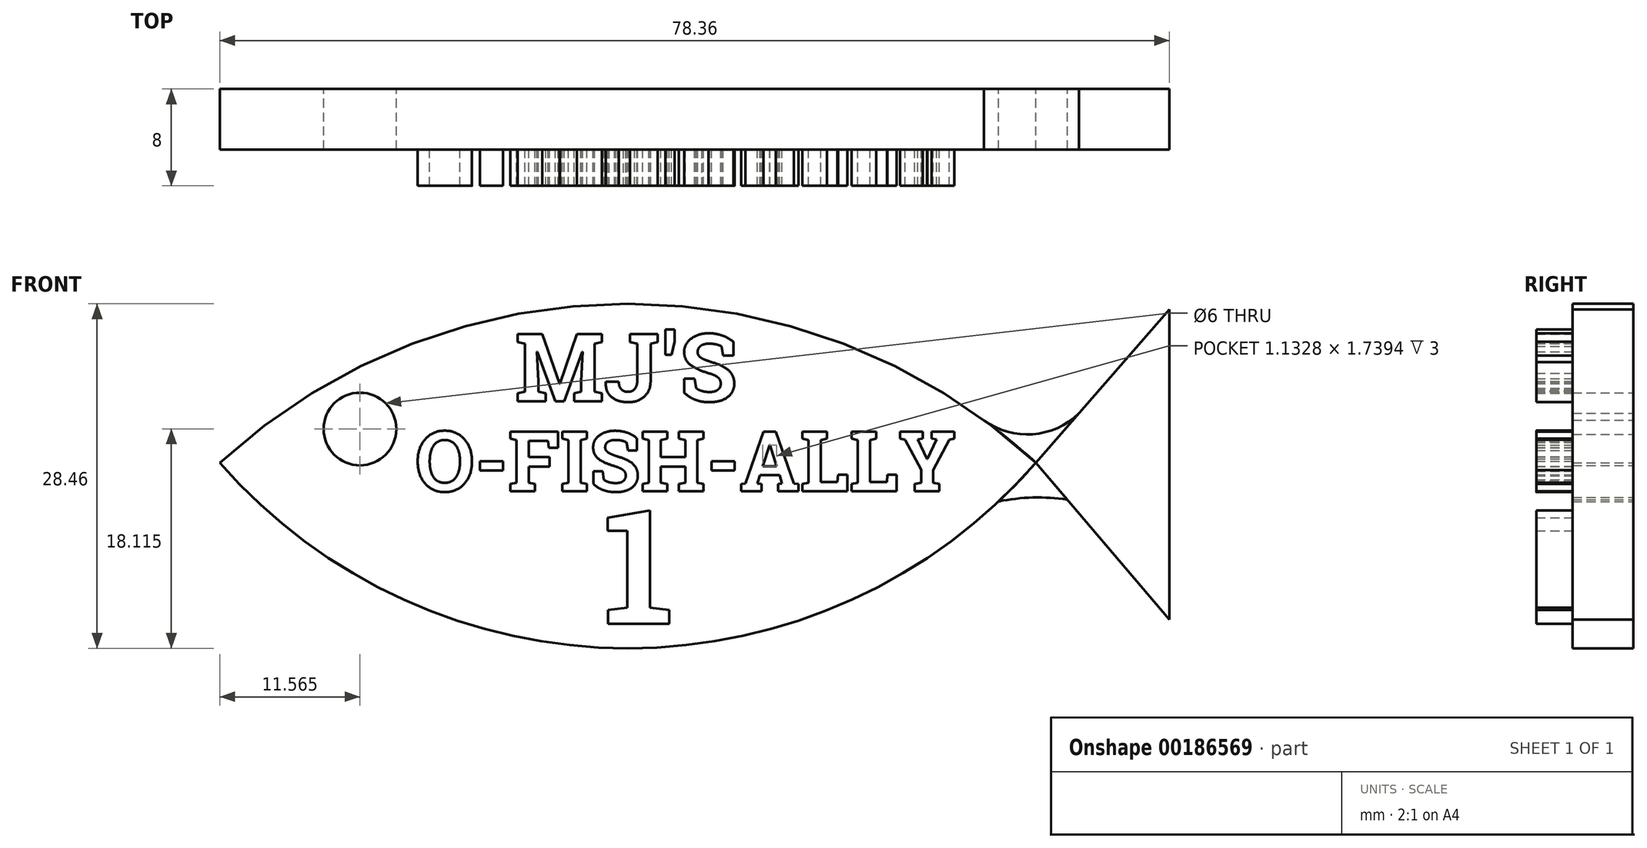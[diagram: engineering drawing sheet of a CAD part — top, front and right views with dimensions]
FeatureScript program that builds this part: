
annotation { "Feature Type Name" : "Feature", "Feature Type Description" : "" }
export const myFeature = defineFeature(function(context is Context, id is Id, definition is map)
    precondition{}
    {
        {
            var Q0;
            Q0=qCreatedBy(makeId("Front.planeOp"),FACE);
            var sketch = newSketch(context, id + "F0", { "sketchPlane" : qUnion([Q0])});
            skLineSegment(sketch, "E0.bottom", {"start": v(0, 0) * mm, "end": v(75, 0) * mm});
            skLineSegment(sketch, "E0.top", {"start": v(0, -25) * mm, "end": v(75, -25) * mm});
            skLineSegment(sketch, "E0.left", {"start": v(0, 0) * mm, "end": v(0, -25) * mm});
            skLineSegment(sketch, "E0.right", {"start": v(75, 0) * mm, "end": v(75, -25) * mm});
            skCircle(sketch, "E1", {"center": v(68, -12.5) * mm, "radius": 3.5 * mm});
            skSolve(sketch);
        }
        {
            var Q0;
            Q0=makeQuery(id+"F0.imprint","IMPRINT",FACE,{"disambiguationData":[TD([[makeQuery(id+"F0.imprint","IMPRINT",EDGE,{"derivedFrom":sQuery(id+"F0.wireOp",EDGE,"E0.bottom")}),-1.0]])]});
            extrude(context, id + "F1", {"entities" : qUnion([Q0]), "depth" : 5 * mm});
        }
        {
            var Q0;
            Q0=makeQuery(id+"F1.opExtrude","CAP_FACE",FACE,{"disambiguationData":[OSD([sQuery(id+"F0.wireOp",EDGE,"E0.bottom"),sQuery(id+"F0.wireOp",EDGE,"E0.top"),sQuery(id+"F0.wireOp",EDGE,"E0.left"),sQuery(id+"F0.wireOp",EDGE,"E0.right"),sQuery(id+"F0.wireOp",EDGE,"E1")])],"isStart":false});
            var sketch = newSketch(context, id + "F2", { "sketchPlane" : qUnion([Q0])});
            skArc(sketch, "E2", {"start": v(33.67, 61.06) * mm, "mid": v(-0.04, 74.19) * mm, "end": v(-33.73, 61) * mm});
            skArc(sketch, "E3", {"start": v(-33.73, 61.13) * mm, "mid": v(-0.05, 45.73) * mm, "end": v(33.67, 61.06) * mm});
            skLineSegment(sketch, "E4", {"start": v(33.67, 61.06) * mm, "end": v(44.7, 73.72) * mm});
            skLineSegment(sketch, "E5", {"start": v(44.7, 73.72) * mm, "end": v(44.7, 48.11) * mm});
            skLineSegment(sketch, "E6", {"start": v(44.7, 48.11) * mm, "end": v(33.67, 61.06) * mm});
            skCircle(sketch, "E7", {"center": v(-22.1, 63.85) * mm, "radius": 3 * mm});
            skArc(sketch, "E8", {"start": v(29.4, 64.57) * mm, "mid": v(33.4, 63.41) * mm, "end": v(37.22, 65.13) * mm});
            skArc(sketch, "E9", {"start": v(36.27, 58) * mm, "mid": v(33.42, 58.18) * mm, "end": v(30.6, 57.86) * mm});
            skSolve(sketch);
        }
        {
            var Q0;
            Q0=makeQuery(id+"F2.imprint","IMPRINT",FACE,{"disambiguationData":[TD([[makeQuery(id+"F2.imprint","IMPRINT",EDGE,{"derivedFrom":sQuery(id+"F2.wireOp",EDGE,"E7")}),-1.0]])]});
            var Q1;
            {var subQ1=sQuery(id+"F2.wireOp",EDGE,"E5");Q1=makeQuery(id+"F2.imprint","IMPRINT",FACE,{"disambiguationData":[TD([[makeQuery(id+"F2.imprint","IMPRINT",EDGE,{"derivedFrom":subQ1}),-1.0]])]});}
            extrude(context, id + "F3", {"entities" : qUnion([Q0, Q1]), "depth" : 5 * mm});
        }
        {
            var Q0;
            {var subQ3=sQuery(id+"F2.wireOp",EDGE,"E8");Q0=makeQuery(id+"F2.imprint","IMPRINT",FACE,{"disambiguationData":[TD([[makeQuery(id+"F2.imprint","IMPRINT",EDGE,{"derivedFrom":subQ3}),-1.0]])]});}
            extrude(context, id + "F4", {"entities" : qUnion([Q0]), "depth" : 5 * mm});
        }
        {
            var Q0;
            {var subQ3=sQuery(id+"F2.wireOp",EDGE,"E9");Q0=makeQuery(id+"F2.imprint","IMPRINT",FACE,{"disambiguationData":[TD([[makeQuery(id+"F2.imprint","IMPRINT",EDGE,{"derivedFrom":subQ3}),-1.0]])]});}
            extrude(context, id + "F5", {"entities" : qUnion([Q0]), "depth" : 5 * mm});
        }
        {
            var Q0;
            Q0=makeQuery(id+"F1.opExtrude","SWEPT_BODY",BODY,{"disambiguationData":[OSD([sQuery(id+"F0.wireOp",EDGE,"E0.bottom"),sQuery(id+"F0.wireOp",EDGE,"E0.top"),sQuery(id+"F0.wireOp",EDGE,"E0.left"),sQuery(id+"F0.wireOp",EDGE,"E0.right"),sQuery(id+"F0.wireOp",EDGE,"E1")])]});
            deleteBodies(context, id + "F6", {"entities" : qUnion([Q0])});
        }
        {
            var Q0;
            Q0=makeQuery(id+"F3.opExtrude","CAP_FACE",FACE,{"disambiguationData":[OSD([sQuery(id+"F2.wireOp",EDGE,"E2"),sQuery(id+"F2.wireOp",EDGE,"E3"),sQuery(id+"F2.wireOp",EDGE,"E7")])],"isStart":false});
            var sketch = newSketch(context, id + "F7", { "sketchPlane" : qUnion([Q0])});
            skText(sketch, "E10", { "text": "MJ\'S", "fontName": "RobotoSlab-Bold.ttf"});
            const initialGuessF7  = {"E10": [-0.0093, 0.06614, 1, 0, 0.00561]};
            skSetInitialGuess(sketch, initialGuessF7);
            skSolve(sketch);
        }
        {
            var Q0;
            Q0 = qSketchRegion(id + "F7", true);
            extrude(context, id + "F8", {"entities" : qUnion([Q0]), "operationType" : NewBodyOperationType.ADD, "depth" : 3 * mm});
        }
        {
            var Q0;
            Q0=makeQuery(id+"F3.opExtrude","CAP_FACE",FACE,{"disambiguationData":[OSD([sQuery(id+"F2.wireOp",EDGE,"E2"),sQuery(id+"F2.wireOp",EDGE,"E3"),sQuery(id+"F2.wireOp",EDGE,"E7")])],"isStart":false});
            var sketch = newSketch(context, id + "F9", { "sketchPlane" : qUnion([Q0])});
            skText(sketch, "E11", { "text": "O-FISH-ALLY", "fontName": "RobotoSlab-Bold.ttf"});
            const initialGuessF9  = {"E11": [-0.01757, 0.0587, 1, 0, 0.005]};
            skSetInitialGuess(sketch, initialGuessF9);
            skSolve(sketch);
        }
        {
            var Q0;
            Q0 = qSketchRegion(id + "F9", true);
            extrude(context, id + "F10", {"entities" : qUnion([Q0]), "operationType" : NewBodyOperationType.ADD, "depth" : 3 * mm});
        }
        {
            var Q0;
            {var subQ0=sQuery(id+"F2.wireOp",EDGE,"E2");var subQ1=sQuery(id+"F2.wireOp",EDGE,"E3");var subQ2=sQuery(id+"F2.wireOp",EDGE,"E7");Q0=makeQuery(id+"F10.boolean.opBoolean","SPLIT",FACE,{"disambiguationData":[TD([makeQuery(id+"F3.opExtrude","SWEPT_FACE",FACE,{"disambiguationData":[OSD([subQ0])]})])],"derivedFrom":makeQuery(id+"F3.opExtrude","CAP_FACE",FACE,{"disambiguationData":[OSD([subQ0,subQ1,subQ2])],"isStart":false})});}
            var sketch = newSketch(context, id + "F11", { "sketchPlane" : qUnion([Q0])});
            skText(sketch, "E12", { "text": "1", "fontName": "RobotoSlab-Bold.ttf"});
            const initialGuessF11  = {"E12": [-0.00206, 0.04775, 1, 0, 0.0095]};
            skSetInitialGuess(sketch, initialGuessF11);
            skSolve(sketch);
        }
        {
            var Q0;
            Q0 = qSketchRegion(id + "F11", true);
            var Q1;
            Q1 = qConstructionFilter(qBodyType(qCreatedBy(id + "F11" ,EDGE), BodyType.WIRE), ConstructionObject.NO);
            extrude(context, id + "F12", {"entities" : qUnion([Q0]), "surfaceEntities" : qUnion([Q1]), "depth" : 3 * mm});
        }
    });
